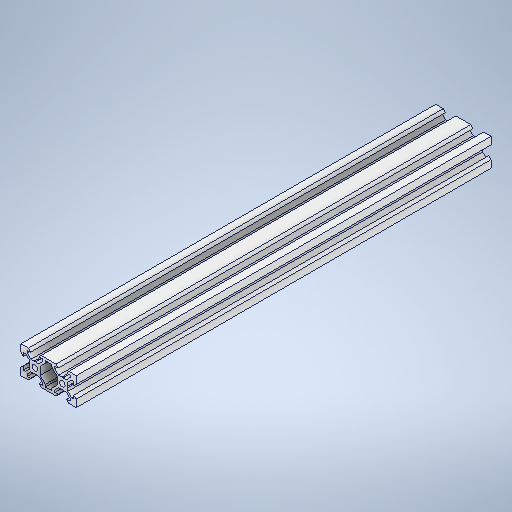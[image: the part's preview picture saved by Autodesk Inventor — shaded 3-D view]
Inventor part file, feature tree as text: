
AUTODESK INVENTOR PART (.ipt)
format: ipt  version: 2025.2 (Build 292293000, 293)  size: 382,976 bytes
history: native  units: in
note: dims shown in document units (in); Inventor stores cm internally (conversion verified against a paired STEP export)
features: plane x2, extrude x1, sketch x1, other x1
ambient origin geometry x8: Origin, YZ Plane, XZ Plane, XY Plane, X Axis, Y Axis, Z Axis, Center Point
bodies: Solid1 (feature_tree)
feature tree (5):
  extrude  "Extrusion1"  [1 undecoded]
  plane  "Work Plane1"
  plane  "Work Plane2"
  sketch  "Sketch1"  dims[d0=7.874in d1=0.0in]
  other  "Boss-Extrude1"
note: 1 required parameter value undecoded (feature->parameter linkage not recoverable at this tier; creation-order binding heuristic only, values carry confidence <= 0.55)
